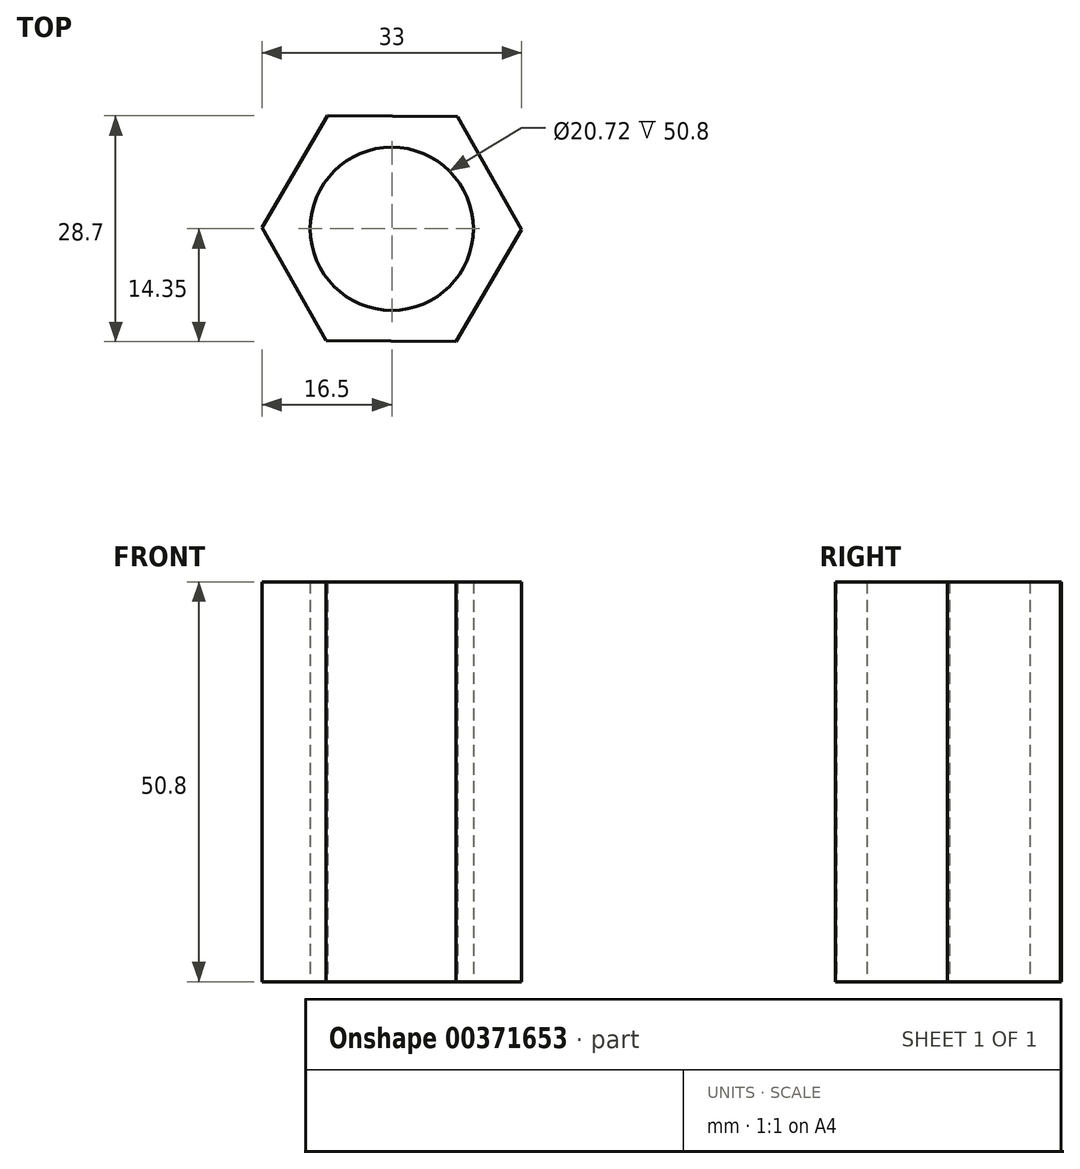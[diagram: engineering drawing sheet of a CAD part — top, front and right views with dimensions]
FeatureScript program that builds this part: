
annotation { "Feature Type Name" : "Feature", "Feature Type Description" : "" }
export const myFeature = defineFeature(function(context is Context, id is Id, definition is map)
    precondition{}
    {
        {
            var Q0;
            Q0=qCreatedBy(makeId("Top.planeOp"),FACE);
            var sketch = newSketch(context, id + "F0", { "sketchPlane" : qUnion([Q0])});
            skCircle(sketch, "E0", {"center": v(0, 0) * mm, "radius": 10.36 * mm});
            skCircle(sketch, "E1.cCircle", {"center": v(0, 0) * mm, "radius": 14.29 * mm, "construction": true});
            skLineSegment(sketch, "E1.0", {"start": v(-16.5, 0.13) * mm, "end": v(-8.14, 14.35) * mm});
            skLineSegment(sketch, "E1.1", {"start": v(-8.14, 14.35) * mm, "end": v(8.36, 14.22) * mm});
            skLineSegment(sketch, "E1.2", {"start": v(8.36, 14.22) * mm, "end": v(16.5, -0.13) * mm});
            skLineSegment(sketch, "E1.3", {"start": v(16.5, -0.13) * mm, "end": v(8.14, -14.35) * mm});
            skLineSegment(sketch, "E1.4", {"start": v(8.14, -14.35) * mm, "end": v(-8.36, -14.22) * mm});
            skLineSegment(sketch, "E1.5", {"start": v(-8.36, -14.22) * mm, "end": v(-16.5, 0.13) * mm});
            skPoint(sketch, "E1.0.midPoint", {"position": v(-12.32, 7.24) * mm});
            skSolve(sketch);
        }
        {
            var Q0;
            Q0 = qSketchRegion(id + "F0", true);
            extrude(context, id + "F1", {"entities" : qUnion([Q0]), "depth" : 25.4 * mm, "hasSecondDirection" : true, "secondDirectionOppositeDirection" : true, "secondDirectionDepth" : 25.4 * mm});
        }
    });
